# Revit family: QF_ELECTROLUXPROFESSIONAL_341089_D10R3
name_source: partatom
category: Specialty Equipment
revit_build: Autodesk Revit 2018 (Build: 20190510_1515(x64)
units: mm (PartAtom-declared; Revit-internal decimal feet)

## family parameters
Always vertical = Yes
Cut with Voids When Loaded = No
Part Type = Normal
Room Calculation Point = No
Round Connector Dimension = Use Diameter
Shared = No
Work Plane-Based = No

## types (2) — shared parameters
Accessory = Yes
Cold Water Size = 0 mm
Compressed Air Pressure = 0.0 Pa
Compressed Air Size = 0 mm
Compressed Air Volume = 0.0 L/s
Condensate Return Size = 0 mm
Depth Actual = 620 mm  [stored 2.03412 ft]
Direct Waste Size = 25 mm
Gas Input Pressure = 0
Gas Size = 0 mm
HP = 0 HP
Height Actual = 260 mm  [stored 0.853018 ft]
Hot Water Size = 0 mm
Length Actual = 1100 mm
Refrigerant Compressor Remote = Yes
Refrigeration Liquid Line Size = 0 mm
Refrigeration Suction Line Size = 0 mm
Steam Supply Maximum Pressure = 0.0 Pa
Steam Supply Minimum Pressure = 0.0 Pa
Steam Supply Size = 0 mm
Watts = 0 W
Weight = 0.00 kg
zero-valued in all types: Gas KW, Steam Pounds per Hour

## per-type parameters (varying)
| type | Cycle | Description | Item Number | Manufacturer | Model | Phase | URL | URL Manufacturer | Volts |
| 341037.rfa | 0 Hz |  |  |  |  | 0 |  |  | 0 V |
| Standard | 50 Hz | DROP-IN REMOTE, REFRIGERATED WELL, STATIC, 3GN | 341089 | Electrolux Professional | D10R3 | 1 | http://professional.electrolux.com | http://professional.electrolux.com | 220 V |

note: source unit labels omitted for Gas Input Pressure — the stored unit's dimension contradicts the parameter name (converter mislabeling)

note: [stored X ft] marks values corroborated as IEEE doubles in the binary element streams (Revit-internal decimal feet)

## geometry (parser evidence)
native form markers: Sweep x5
no freeform markers — native parametric forms only
